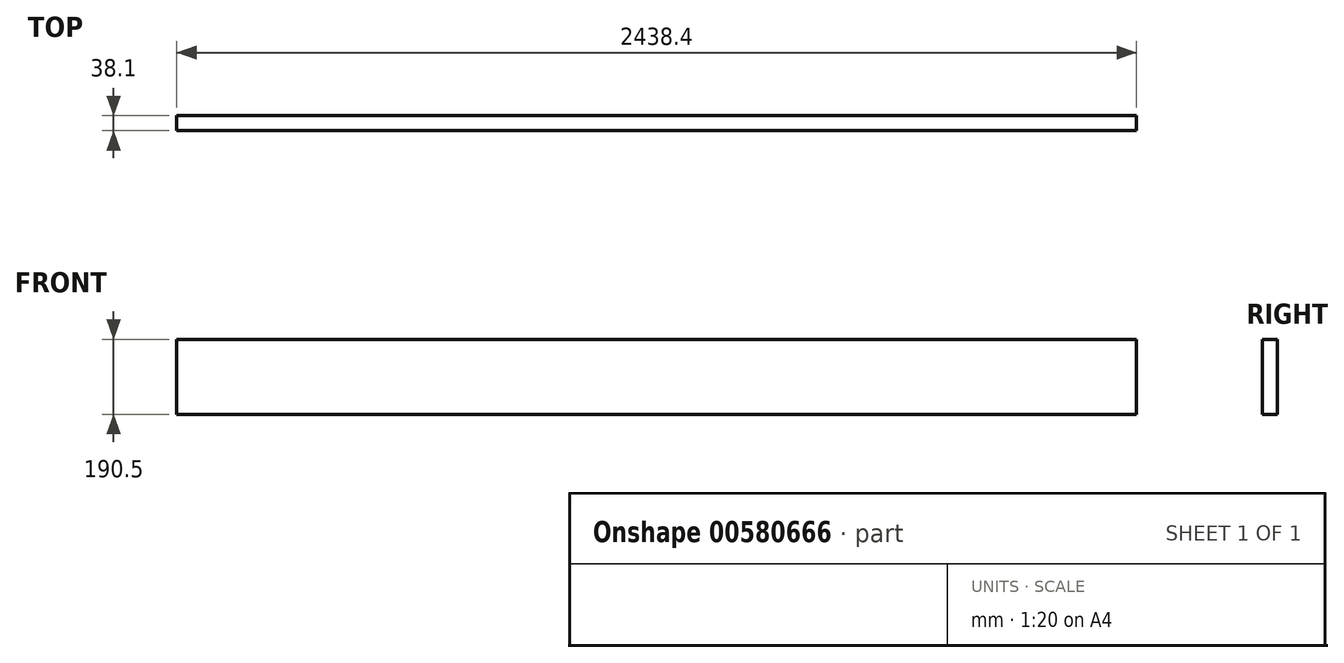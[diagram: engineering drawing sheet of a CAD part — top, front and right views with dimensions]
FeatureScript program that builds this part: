
annotation { "Feature Type Name" : "Feature", "Feature Type Description" : "" }
export const myFeature = defineFeature(function(context is Context, id is Id, definition is map)
    precondition{}
    {
        {
            var Q0;
            Q0=qCreatedBy(makeId("Top.planeOp"),FACE);
            var sketch = newSketch(context, id + "F0", { "sketchPlane" : qUnion([Q0])});
            skLineSegment(sketch, "E0.bottom", {"start": v(1219.2, -19.05) * mm, "end": v(-1219.2, -19.05) * mm});
            skLineSegment(sketch, "E0.top", {"start": v(1219.2, 19.05) * mm, "end": v(-1219.2, 19.05) * mm});
            skLineSegment(sketch, "E0.left", {"start": v(1219.2, -19.05) * mm, "end": v(1219.2, 19.05) * mm});
            skLineSegment(sketch, "E0.right", {"start": v(-1219.2, -19.05) * mm, "end": v(-1219.2, 19.05) * mm});
            skPoint(sketch, "E0.middle", {"position": v(0, 0) * mm});
            skSolve(sketch);
        }
        {
            var Q0;
            Q0=makeQuery(id+"F0.imprint","IMPRINT",FACE,{"disambiguationData":[TD([[makeQuery(id+"F0.imprint","IMPRINT",EDGE,{"derivedFrom":sQuery(id+"F0.wireOp",EDGE,"E0.bottom")}),-1.0]])]});
            extrude(context, id + "F1", {"entities" : qUnion([Q0]), "depth" : 190.5 * mm, "offsetDistance" : 25.4 * mm});
        }
    });
